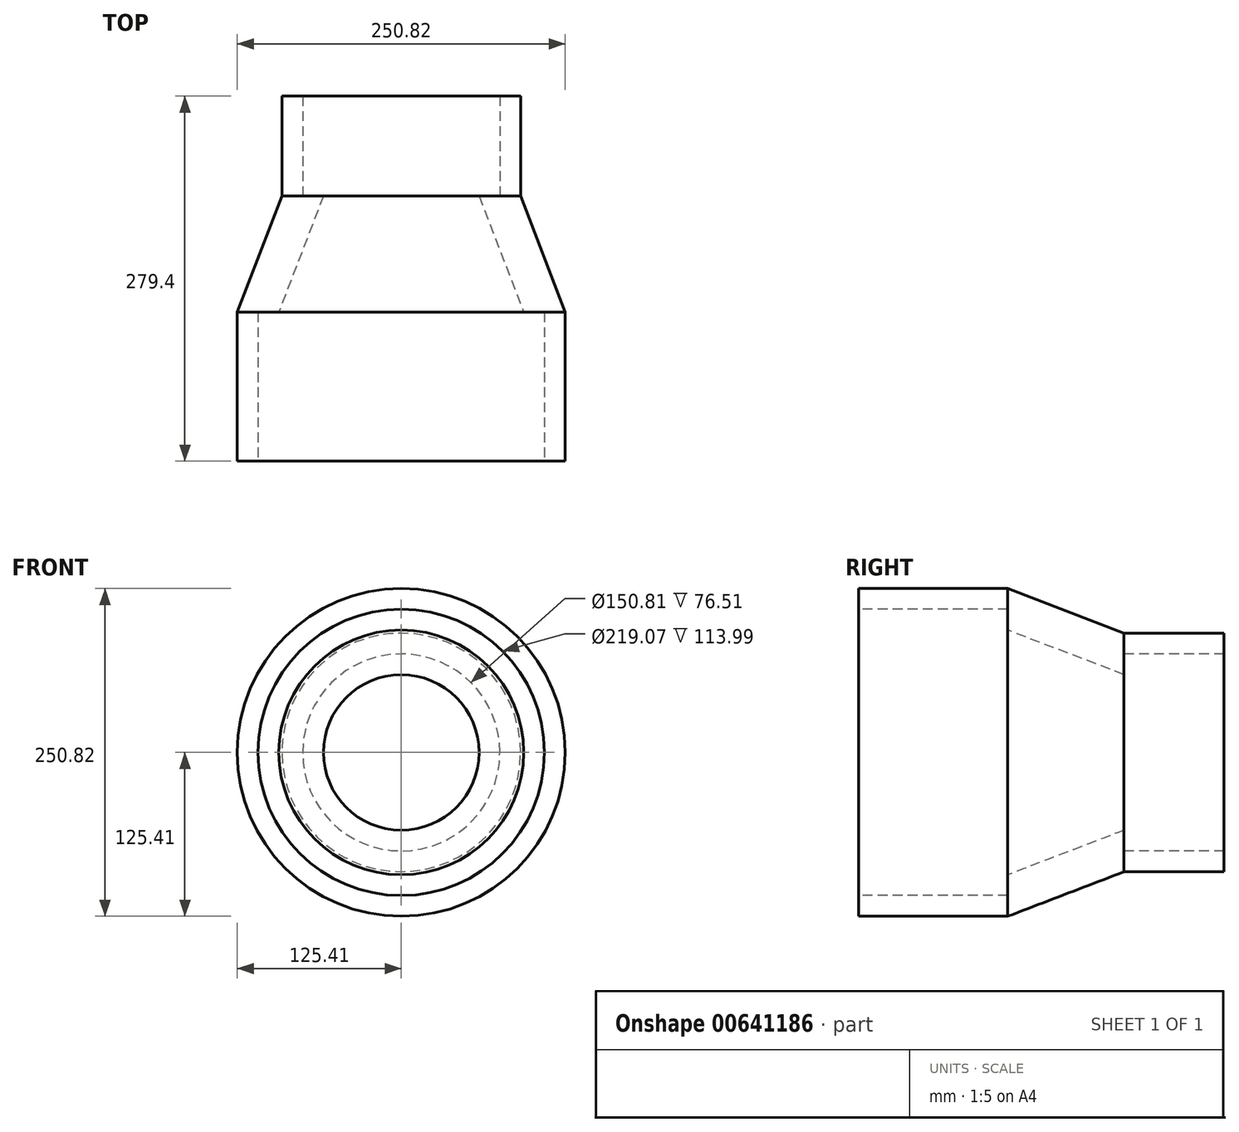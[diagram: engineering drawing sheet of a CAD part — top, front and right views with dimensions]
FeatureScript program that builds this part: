
annotation { "Feature Type Name" : "Feature", "Feature Type Description" : "" }
export const myFeature = defineFeature(function(context is Context, id is Id, definition is map)
    precondition{}
    {
        {
            var Q0;
            Q0=qCreatedBy(makeId("Right.planeOp"),FACE);
            var sketch = newSketch(context, id + "F0", { "sketchPlane" : qUnion([Q0])});
            skLineSegment(sketch, "E0", {"start": v(-157.06, 107.48) * mm, "end": v(-43.07, 107.48) * mm});
            skLineSegment(sketch, "E1", {"start": v(-157.06, -17.93) * mm, "end": v(122.34, -17.93) * mm});
            skLineSegment(sketch, "E2", {"start": v(122.34, -17.93) * mm, "end": v(122.34, 73.35) * mm});
            skLineSegment(sketch, "E3", {"start": v(122.34, 73.35) * mm, "end": v(45.83, 73.35) * mm});
            skLineSegment(sketch, "E4.0", {"start": v(-157.06, 91.6) * mm, "end": v(-43.07, 91.6) * mm});
            skLineSegment(sketch, "E5.0", {"start": v(122.34, 57.48) * mm, "end": v(45.83, 57.48) * mm});
            skLineSegment(sketch, "E6", {"start": v(-43.07, 107.48) * mm, "end": v(45.83, 73.35) * mm});
            skLineSegment(sketch, "E7", {"start": v(-43.07, 91.6) * mm, "end": v(-43.07, 75.73) * mm});
            skLineSegment(sketch, "E8", {"start": v(45.83, 57.48) * mm, "end": v(45.83, 41.6) * mm});
            skLineSegment(sketch, "E9", {"start": v(-43.07, 75.73) * mm, "end": v(45.83, 41.6) * mm});
            skLineSegment(sketch, "E10", {"start": v(-157.06, 107.48) * mm, "end": v(-157.06, 91.6) * mm});
            skSolve(sketch);
        }
        {
            var Q0;
            Q0=makeQuery(id+"F0.imprint","IMPRINT",FACE,{"disambiguationData":[TD([[makeQuery(id+"F0.imprint","IMPRINT",EDGE,{"derivedFrom":sQuery(id+"F0.wireOp",EDGE,"E0")}),-1.0]])]});
            var Q1;
            Q1=sQuery(id+"F0.wireOp",EDGE,"E1");
            revolve(context, id + "F1", {"entities" : qUnion([Q0]), "axis" : qUnion([Q1]), "revolveType" : RevolveType.FULL});
        }
    });
